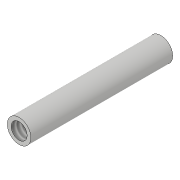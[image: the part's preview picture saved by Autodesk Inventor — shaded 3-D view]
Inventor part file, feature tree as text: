
AUTODESK INVENTOR PART (.ipt)
format: ipt  version: 2018.3 (Build 223284000, 284)  size: 80,896 bytes
history: native  units: in
note: dims shown in document units (in); Inventor stores cm internally (conversion verified against a paired STEP export)
features: extrude x1, hole x1, sketch x1
ambient origin geometry x8: Origin, YZ Plane, XZ Plane, XY Plane, X Axis, Y Axis, Z Axis, Center Point
bodies: Solid1 (feature_tree)
feature tree (3):
  extrude  "Extrusion1"  Depth=0.75in TaperAngle=0.0deg
  hole  "Hole1"  [1 undecoded]
  sketch  "Sketch1"  dims[d0=0.125in d2=0.75in d3=0.0in d15=1.0in d16=1.0in d6=0.085in d7=0.75in d8=0.375in d9=0.25in d10=0.5635in d11=0.349in d12=0.8108in]
note: 1 required parameter value undecoded (feature->parameter linkage not recoverable at this tier; creation-order binding heuristic only, values carry confidence <= 0.55)
